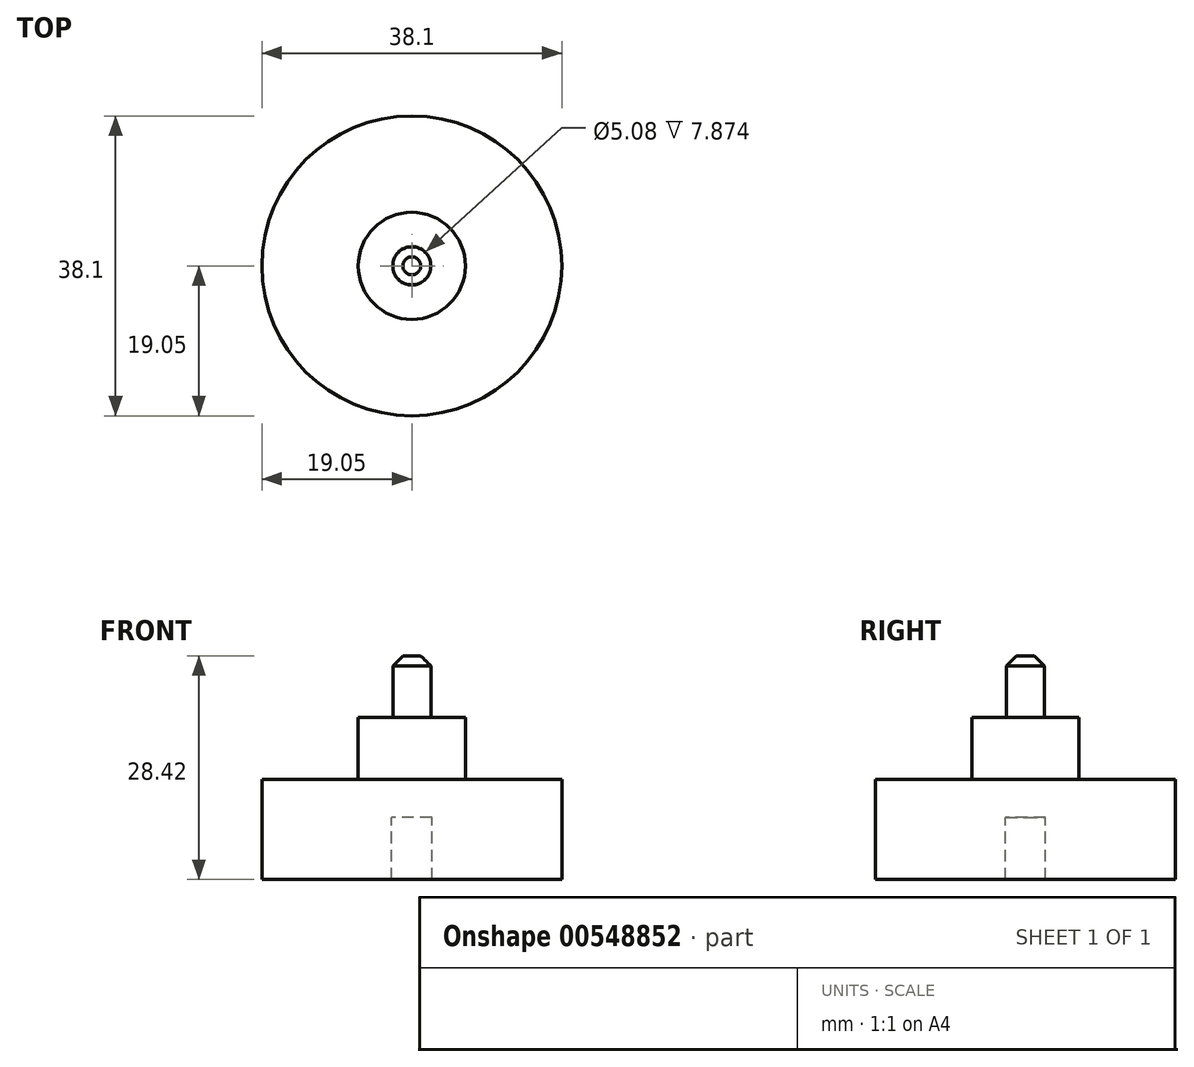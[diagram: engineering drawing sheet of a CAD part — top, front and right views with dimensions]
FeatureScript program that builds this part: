
annotation { "Feature Type Name" : "Feature", "Feature Type Description" : "" }
export const myFeature = defineFeature(function(context is Context, id is Id, definition is map)
    precondition{}
    {
        {
            var Q0;
            Q0=qCreatedBy(makeId("Front.planeOp"),FACE);
            var sketch = newSketch(context, id + "F0", { "sketchPlane" : qUnion([Q0])});
            skLineSegment(sketch, "E0", {"start": v(19.05, 0) * mm, "end": v(19.05, 12.7) * mm});
            skLineSegment(sketch, "E1", {"start": v(19.05, 12.7) * mm, "end": v(6.8, 12.7) * mm});
            skLineSegment(sketch, "E2", {"start": v(2.41, 20.57) * mm, "end": v(6.8, 20.57) * mm});
            skLineSegment(sketch, "E3", {"start": v(6.8, 20.57) * mm, "end": v(6.8, 12.7) * mm});
            skPoint(sketch, "E4.start.orphan", {"position": v(0, 12.7) * mm});
            skLineSegment(sketch, "E5", {"start": v(0, 28.42) * mm, "end": v(2.41, 28.42) * mm});
            skLineSegment(sketch, "E6", {"start": v(2.41, 28.42) * mm, "end": v(2.41, 20.57) * mm});
            skLineSegment(sketch, "E7", {"start": v(2.54, 0) * mm, "end": v(2.54, 7.87) * mm});
            skLineSegment(sketch, "E8", {"start": v(2.54, 7.87) * mm, "end": v(0, 7.87) * mm});
            skLineSegment(sketch, "E9", {"start": v(0, 28.42) * mm, "end": v(0, 7.87) * mm});
            skLineSegment(sketch, "E10", {"start": v(19.05, 0) * mm, "end": v(2.54, 0) * mm});
            skSolve(sketch);
        }
        {
            var Q0;
            Q0 = qSketchRegion(id + "F0", true);
            var Q1;
            Q1=sQuery(id+"F0.wireOp",EDGE,"E9");
            revolve(context, id + "F1", {"entities" : qUnion([Q0]), "axis" : qUnion([Q1]), "revolveType" : RevolveType.FULL});
        }
        {
            var Q0;
            Q0=makeQuery(id+"F1.opRevolve","SWEPT_EDGE",EDGE,{"disambiguationData":[OSD([sQuery(id+"F0.wireOp",EDGE,"E5"),sQuery(id+"F0.wireOp",EDGE,"E6")])]});
            chamfer(context, id + "F2", {"entities" : qUnion([Q0]), "width" : 1.27 * mm, "tangentPropagation" : true});
        }
    });
